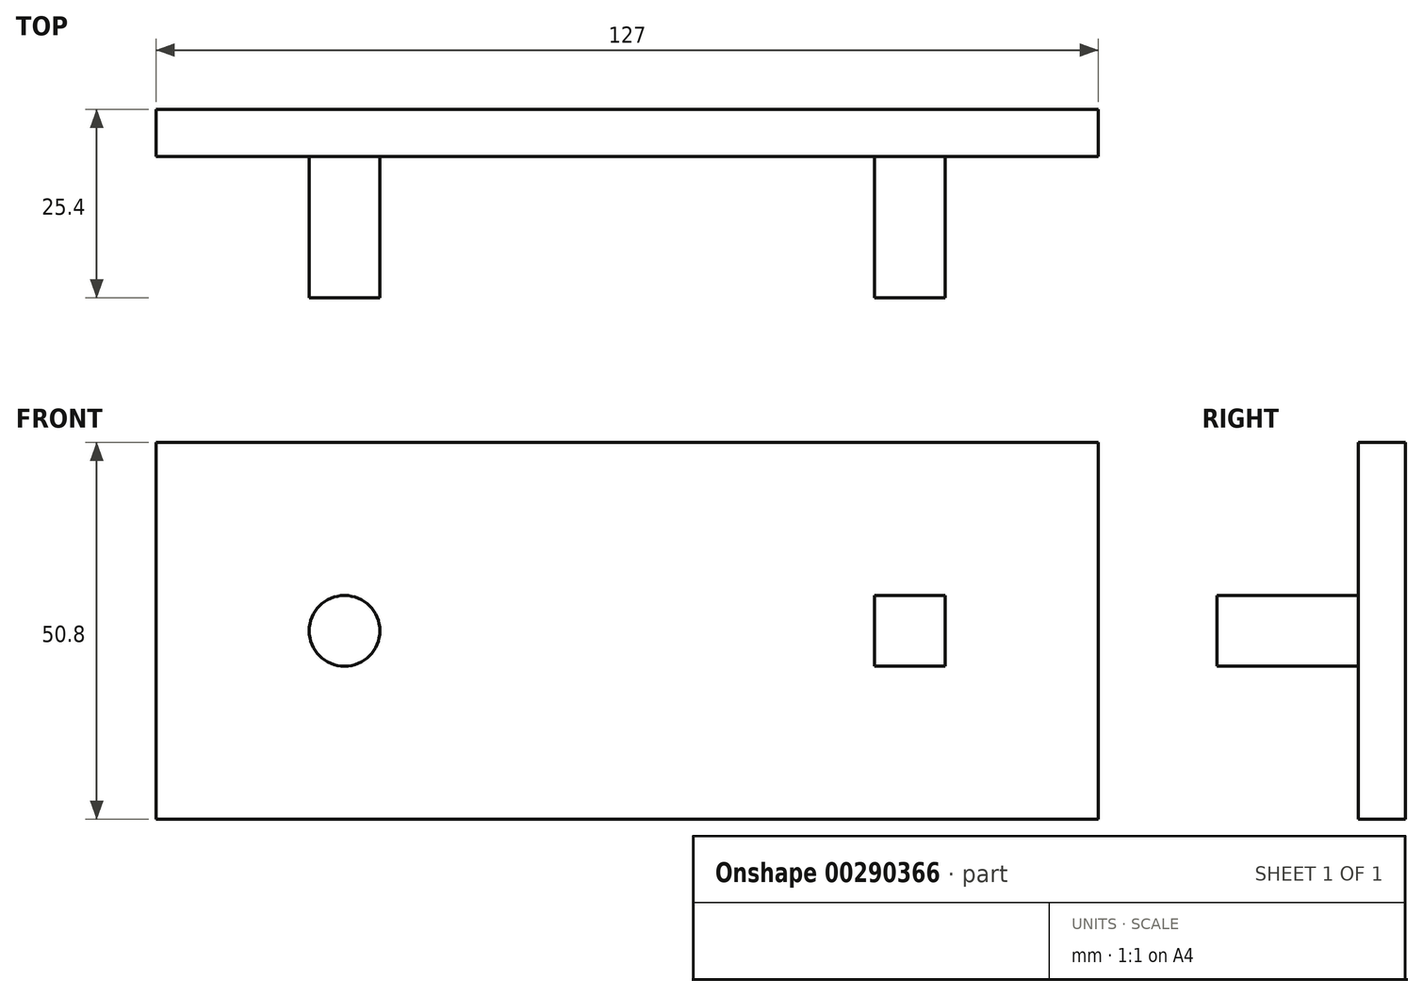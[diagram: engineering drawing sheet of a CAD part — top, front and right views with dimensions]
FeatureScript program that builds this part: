
annotation { "Feature Type Name" : "Feature", "Feature Type Description" : "" }
export const myFeature = defineFeature(function(context is Context, id is Id, definition is map)
    precondition{}
    {
        {
            var Q0;
            Q0=qCreatedBy(makeId("Front.planeOp"),FACE);
            var sketch = newSketch(context, id + "F0", { "sketchPlane" : qUnion([Q0])});
            skLineSegment(sketch, "E0.top", {"start": v(-63.5, -25.4) * mm, "end": v(63.5, -25.4) * mm});
            skLineSegment(sketch, "E0.left", {"start": v(-63.5, 25.4) * mm, "end": v(-63.5, -25.4) * mm});
            skLineSegment(sketch, "E0.right", {"start": v(63.5, 25.4) * mm, "end": v(63.5, -25.4) * mm});
            skLineSegment(sketch, "E1", {"start": v(-63.5, 25.4) * mm, "end": v(63.5, 25.4) * mm});
            skPoint(sketch, "E2", {"position": v(-63.5, 0) * mm});
            skPoint(sketch, "E3", {"position": v(0, 25.4) * mm});
            skLineSegment(sketch, "E4.bottom", {"start": v(33.34, 4.76) * mm, "end": v(42.86, 4.76) * mm});
            skLineSegment(sketch, "E4.top", {"start": v(33.34, -4.76) * mm, "end": v(42.86, -4.76) * mm});
            skLineSegment(sketch, "E4.left", {"start": v(33.34, 4.76) * mm, "end": v(33.34, -4.76) * mm});
            skLineSegment(sketch, "E4.right", {"start": v(42.86, 4.76) * mm, "end": v(42.86, -4.76) * mm});
            skPoint(sketch, "E5", {"position": v(38.1, 0) * mm});
            skPoint(sketch, "E5.positionSnap0", {"position": v(38.1, 4.76) * mm});
            skPoint(sketch, "E5.positionSnap1", {"position": v(42.86, 0) * mm});
            skCircle(sketch, "E6", {"center": v(-38.1, 0) * mm, "radius": 4.76 * mm});
            skSolve(sketch);
        }
        {
            var Q0;
            Q0 = qSketchRegion(id + "F0", true);
            var Q1;
            Q1=makeQuery(id+"F0.imprint","IMPRINT",FACE,{"disambiguationData":[TD([[makeQuery(id+"F0.imprint","IMPRINT",EDGE,{"derivedFrom":sQuery(id+"F0.wireOp",EDGE,"E6")}),1.0]])]});
            var Q2;
            Q2=makeQuery(id+"F0.imprint","IMPRINT",FACE,{"disambiguationData":[TD([[makeQuery(id+"F0.imprint","IMPRINT",EDGE,{"derivedFrom":sQuery(id+"F0.wireOp",EDGE,"E4.bottom")}),-1.0]])]});
            extrude(context, id + "F1", {"entities" : qUnion([Q0, Q1, Q2]), "oppositeDirection" : true, "depth" : 6.35 * mm});
        }
        {
            var Q0;
            Q0=makeQuery(id+"F0.imprint","IMPRINT",FACE,{"disambiguationData":[TD([[makeQuery(id+"F0.imprint","IMPRINT",EDGE,{"derivedFrom":sQuery(id+"F0.wireOp",EDGE,"E6")}),1.0]])]});
            var Q1;
            Q1=makeQuery(id+"F0.imprint","IMPRINT",FACE,{"disambiguationData":[TD([[makeQuery(id+"F0.imprint","IMPRINT",EDGE,{"derivedFrom":sQuery(id+"F0.wireOp",EDGE,"E4.bottom")}),-1.0]])]});
            extrude(context, id + "F2", {"entities" : qUnion([Q0, Q1]), "operationType" : NewBodyOperationType.ADD, "depth" : 19.05 * mm});
        }
    });
